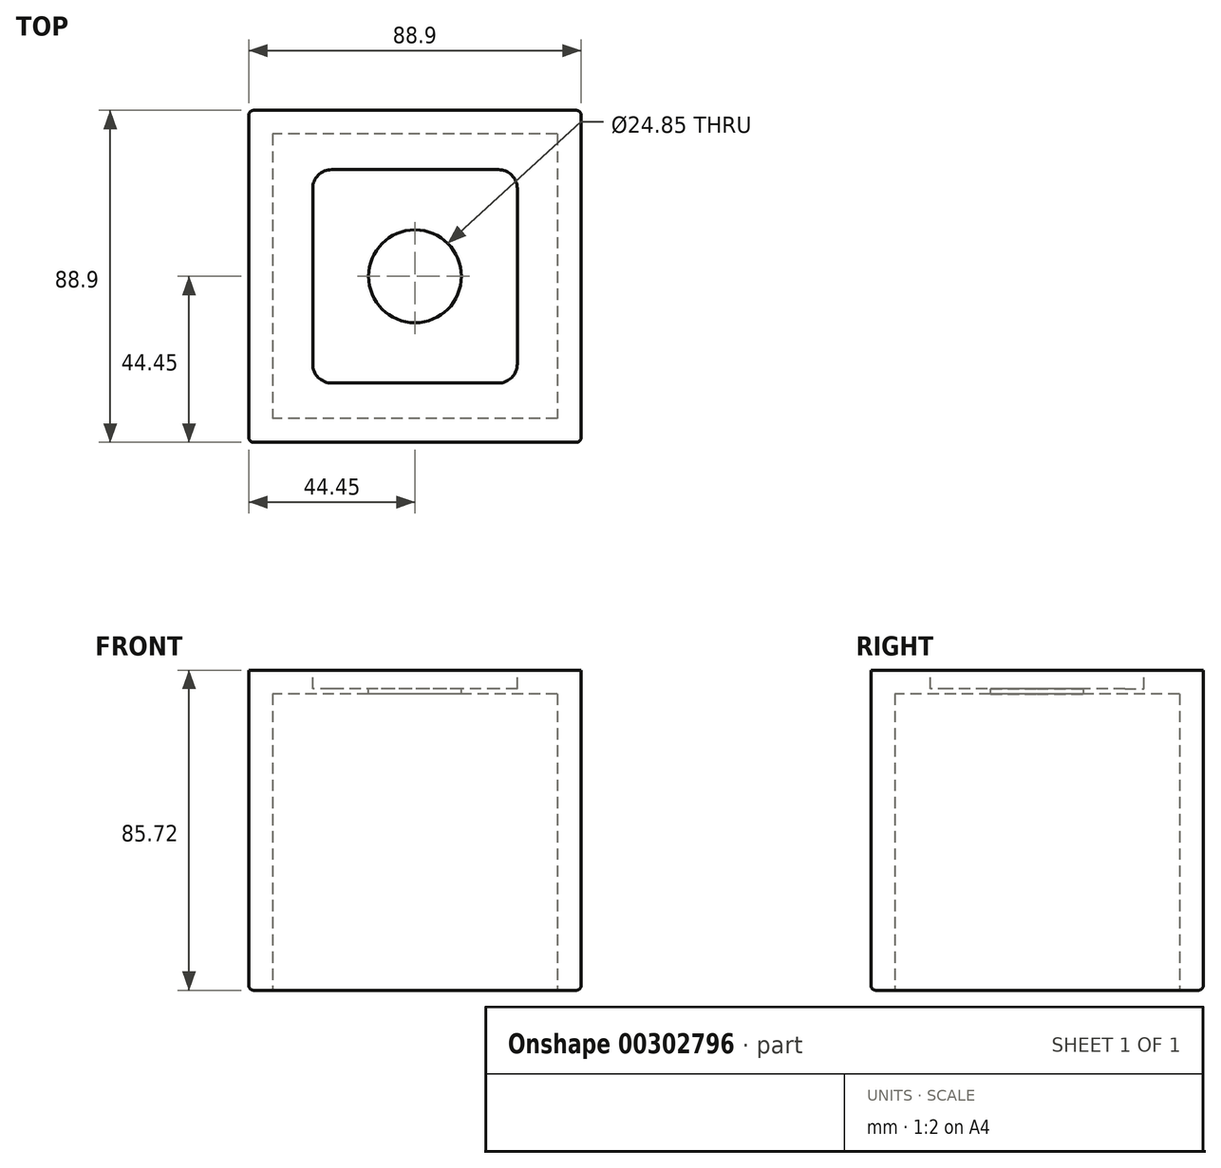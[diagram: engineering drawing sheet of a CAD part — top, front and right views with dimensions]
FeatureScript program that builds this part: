
annotation { "Feature Type Name" : "Feature", "Feature Type Description" : "" }
export const myFeature = defineFeature(function(context is Context, id is Id, definition is map)
    precondition{}
    {
        {
            var Q0;
            Q0=qCreatedBy(makeId("Top.planeOp"),FACE);
            var sketch = newSketch(context, id + "F0", { "sketchPlane" : qUnion([Q0])});
            skLineSegment(sketch, "E0.bottom", {"start": v(44.45, 44.45) * mm, "end": v(-44.45, 44.45) * mm});
            skLineSegment(sketch, "E0.top", {"start": v(44.45, -44.45) * mm, "end": v(-44.45, -44.45) * mm});
            skLineSegment(sketch, "E0.left", {"start": v(44.45, 44.45) * mm, "end": v(44.45, -44.45) * mm});
            skLineSegment(sketch, "E0.right", {"start": v(-44.45, 44.45) * mm, "end": v(-44.45, -44.45) * mm});
            skPoint(sketch, "E0.middle", {"position": v(0, 0) * mm});
            skSolve(sketch);
        }
        {
            var Q0;
            Q0 = qSketchRegion(id + "F0", true);
            extrude(context, id + "F1", {"entities" : qUnion([Q0]), "depth" : 85.72 * mm});
        }
        {
            var Q0;
            Q0=makeQuery(id+"F1.opExtrude","CAP_FACE",FACE,{"disambiguationData":[OSD([sQuery(id+"F0.wireOp",EDGE,"E0.bottom"),sQuery(id+"F0.wireOp",EDGE,"E0.top"),sQuery(id+"F0.wireOp",EDGE,"E0.left"),sQuery(id+"F0.wireOp",EDGE,"E0.right")])],"isStart":true});
            shell(context, id + "F2", {"entities" : qUnion([Q0]), "thickness" : 6.35 * mm});
        }
        {
            var Q0;
            Q0=makeQuery(id+"F1.opExtrude","CAP_FACE",FACE,{"disambiguationData":[OSD([sQuery(id+"F0.wireOp",EDGE,"E0.bottom"),sQuery(id+"F0.wireOp",EDGE,"E0.top"),sQuery(id+"F0.wireOp",EDGE,"E0.left"),sQuery(id+"F0.wireOp",EDGE,"E0.right")])],"isStart":false});
            var sketch = newSketch(context, id + "F3", { "sketchPlane" : qUnion([Q0])});
            skLineSegment(sketch, "E1.bottom", {"start": v(27.36, 28.58) * mm, "end": v(-27.36, 28.58) * mm});
            skLineSegment(sketch, "E1.top", {"start": v(27.36, -28.58) * mm, "end": v(-27.36, -28.58) * mm});
            skLineSegment(sketch, "E1.left", {"start": v(27.36, 28.58) * mm, "end": v(27.36, -28.58) * mm});
            skLineSegment(sketch, "E1.right", {"start": v(-27.36, 28.58) * mm, "end": v(-27.36, -28.58) * mm});
            skPoint(sketch, "E1.middle", {"position": v(0, 0) * mm});
            skSolve(sketch);
        }
        {
            var Q0;
            Q0 = qSketchRegion(id + "F3", true);
            extrude(context, id + "F4", {"entities" : qUnion([Q0]), "operationType" : NewBodyOperationType.REMOVE, "oppositeDirection" : true, "depth" : 5 * mm});
        }
        {
            var Q0;
            Q0=makeQuery(id+"F4.boolean.opBoolean","COPY",EDGE,{"derivedFrom":makeQuery(id+"F4.opExtrude","SWEPT_EDGE",EDGE,{"disambiguationData":[OSD([sQuery(id+"F3.wireOp",EDGE,"E1.bottom"),sQuery(id+"F3.wireOp",EDGE,"E1.right")])]})});
            var Q1;
            Q1=makeQuery(id+"F4.boolean.opBoolean","COPY",EDGE,{"derivedFrom":makeQuery(id+"F4.opExtrude","SWEPT_EDGE",EDGE,{"disambiguationData":[OSD([sQuery(id+"F3.wireOp",EDGE,"E1.top"),sQuery(id+"F3.wireOp",EDGE,"E1.right")])]})});
            var Q2;
            Q2=makeQuery(id+"F4.boolean.opBoolean","COPY",EDGE,{"derivedFrom":makeQuery(id+"F4.opExtrude","SWEPT_EDGE",EDGE,{"disambiguationData":[OSD([sQuery(id+"F3.wireOp",EDGE,"E1.top"),sQuery(id+"F3.wireOp",EDGE,"E1.left")])]})});
            var Q3;
            Q3=makeQuery(id+"F4.boolean.opBoolean","COPY",EDGE,{"derivedFrom":makeQuery(id+"F4.opExtrude","SWEPT_EDGE",EDGE,{"disambiguationData":[OSD([sQuery(id+"F3.wireOp",EDGE,"E1.bottom"),sQuery(id+"F3.wireOp",EDGE,"E1.left")])]})});
            fillet(context, id + "F5", {"entities" : qUnion([Q0, Q1, Q2, Q3]), "radius" : 5.08 * mm, "tangentPropagation" : true, "allowEdgeOverflow" : false});
        }
        {
            var Q0;
            Q0=makeQuery(id+"F1.opExtrude","SWEPT_EDGE",EDGE,{"disambiguationData":[OSD([sQuery(id+"F0.wireOp",EDGE,"E0.top"),sQuery(id+"F0.wireOp",EDGE,"E0.left")])]});
            var Q1;
            Q1=makeQuery(id+"F1.opExtrude","SWEPT_EDGE",EDGE,{"disambiguationData":[OSD([sQuery(id+"F0.wireOp",EDGE,"E0.bottom"),sQuery(id+"F0.wireOp",EDGE,"E0.left")])]});
            var Q2;
            Q2=makeQuery(id+"F1.opExtrude","SWEPT_EDGE",EDGE,{"disambiguationData":[OSD([sQuery(id+"F0.wireOp",EDGE,"E0.top"),sQuery(id+"F0.wireOp",EDGE,"E0.right")])]});
            var Q3;
            Q3=makeQuery(id+"F1.opExtrude","SWEPT_EDGE",EDGE,{"disambiguationData":[OSD([sQuery(id+"F0.wireOp",EDGE,"E0.bottom"),sQuery(id+"F0.wireOp",EDGE,"E0.right")])]});
            var Q4;
            Q4=makeQuery(id+"F1.opExtrude","CAP_EDGE",EDGE,{"disambiguationData":[OSD([sQuery(id+"F0.wireOp",EDGE,"E0.right")])],"isStart":true});
            var Q5;
            Q5=makeQuery(id+"F1.opExtrude","CAP_EDGE",EDGE,{"disambiguationData":[OSD([sQuery(id+"F0.wireOp",EDGE,"E0.top")])],"isStart":true});
            var Q6;
            Q6=makeQuery(id+"F1.opExtrude","CAP_EDGE",EDGE,{"disambiguationData":[OSD([sQuery(id+"F0.wireOp",EDGE,"E0.bottom")])],"isStart":true});
            var Q7;
            Q7=makeQuery(id+"F1.opExtrude","CAP_EDGE",EDGE,{"disambiguationData":[OSD([sQuery(id+"F0.wireOp",EDGE,"E0.left")])],"isStart":true});
            fillet(context, id + "F6", {"entities" : qUnion([Q0, Q1, Q2, Q3, Q4, Q5, Q6, Q7]), "radius" : 1.27 * mm, "tangentPropagation" : true, "allowEdgeOverflow" : false});
        }
        {
            var Q0;
            Q0=makeQuery(id+"F4.boolean.opBoolean","COPY",FACE,{"derivedFrom":makeQuery(id+"F4.opExtrude","CAP_FACE",FACE,{"disambiguationData":[OSD([sQuery(id+"F3.wireOp",EDGE,"E1.bottom"),sQuery(id+"F3.wireOp",EDGE,"E1.top"),sQuery(id+"F3.wireOp",EDGE,"E1.left"),sQuery(id+"F3.wireOp",EDGE,"E1.right")])],"isStart":false})});
            var sketch = newSketch(context, id + "F7", { "sketchPlane" : qUnion([Q0])});
            skCircle(sketch, "E2", {"center": v(0, 0) * mm, "radius": 12.43 * mm});
            skSolve(sketch);
        }
        {
            var Q0;
            Q0 = qSketchRegion(id + "F7", true);
            extrude(context, id + "F8", {"entities" : qUnion([Q0]), "operationType" : NewBodyOperationType.REMOVE, "oppositeDirection" : true, "depth" : 25.4 * mm});
        }
    });
